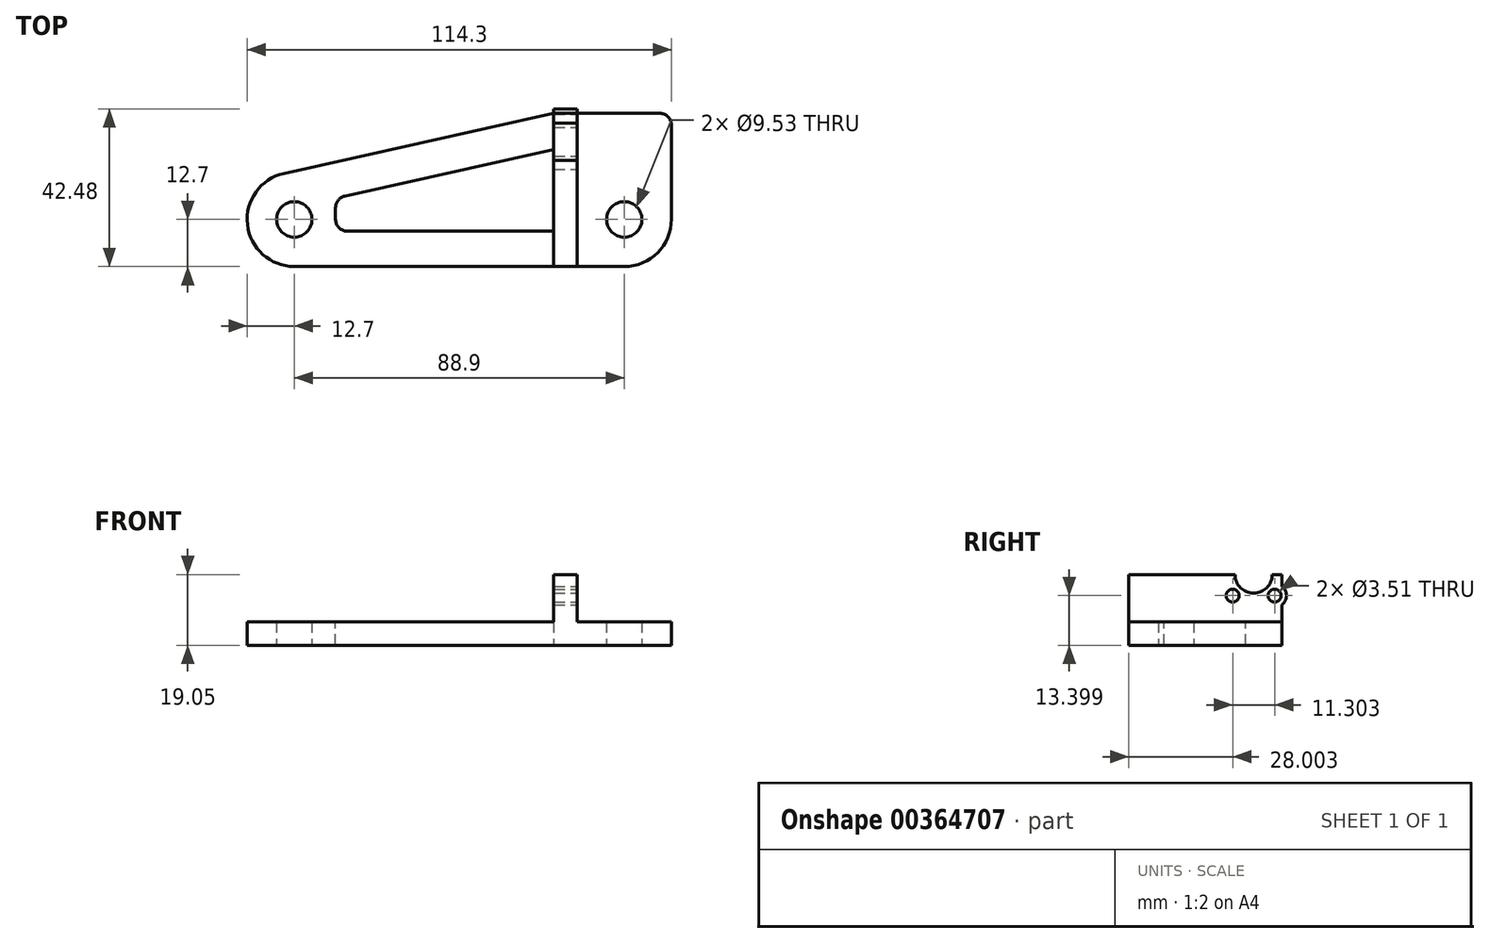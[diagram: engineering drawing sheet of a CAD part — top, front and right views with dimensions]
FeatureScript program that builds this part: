
annotation { "Feature Type Name" : "Feature", "Feature Type Description" : "" }
export const myFeature = defineFeature(function(context is Context, id is Id, definition is map)
    precondition{}
    {
        {
            var Q0;
            Q0=qCreatedBy(makeId("Top.planeOp"),FACE);
            var sketch = newSketch(context, id + "F0", { "sketchPlane" : qUnion([Q0])});
            skCircle(sketch, "E0", {"center": v(0, 0) * mm, "radius": 4.76 * mm});
            skCircle(sketch, "E1", {"center": v(-88.9, 0) * mm, "radius": 4.76 * mm});
            skLineSegment(sketch, "E2", {"start": v(12.7, -12.7) * mm, "end": v(-101.6, -12.7) * mm});
            skLineSegment(sketch, "E3", {"start": v(-101.6, -12.7) * mm, "end": v(-101.6, 10.18) * mm});
            skLineSegment(sketch, "E4", {"start": v(-101.6, 10.18) * mm, "end": v(-19.05, 28.58) * mm});
            skLineSegment(sketch, "E5", {"start": v(-19.05, 28.58) * mm, "end": v(12.7, 28.58) * mm});
            skLineSegment(sketch, "E6", {"start": v(12.7, 28.58) * mm, "end": v(12.7, -12.7) * mm});
            skSolve(sketch);
        }
        {
            var Q0;
            Q0 = qSketchRegion(id + "F0", true);
            extrude(context, id + "F1", {"entities" : qUnion([Q0]), "depth" : 6.35 * mm, "offsetDistance" : 25.4 * mm});
        }
        {
            var Q0;
            Q0=makeQuery(id+"F1.opExtrude","SWEPT_EDGE",EDGE,{"disambiguationData":[OSD([sQuery(id+"F0.wireOp",EDGE,"E2"),sQuery(id+"F0.wireOp",EDGE,"E6")])]});
            var Q1;
            Q1=makeQuery(id+"F1.opExtrude","SWEPT_EDGE",EDGE,{"disambiguationData":[OSD([sQuery(id+"F0.wireOp",EDGE,"E2"),sQuery(id+"F0.wireOp",EDGE,"E3")])]});
            var Q2;
            Q2=makeQuery(id+"F1.opExtrude","SWEPT_EDGE",EDGE,{"disambiguationData":[OSD([sQuery(id+"F0.wireOp",EDGE,"E3"),sQuery(id+"F0.wireOp",EDGE,"E4")])]});
            fillet(context, id + "F2", {"entities" : qUnion([Q0, Q1, Q2]), "radius" : 12.7 * mm, "tangentPropagation" : true, "allowEdgeOverflow" : false});
        }
        {
            var Q0;
            Q0=makeQuery(id+"F1.opExtrude","CAP_FACE",FACE,{"disambiguationData":[OSD([sQuery(id+"F0.wireOp",EDGE,"E0"),sQuery(id+"F0.wireOp",EDGE,"E1"),sQuery(id+"F0.wireOp",EDGE,"E2"),sQuery(id+"F0.wireOp",EDGE,"E3"),sQuery(id+"F0.wireOp",EDGE,"E4"),sQuery(id+"F0.wireOp",EDGE,"E5"),sQuery(id+"F0.wireOp",EDGE,"E6")])],"isStart":false});
            var sketch = newSketch(context, id + "F3", { "sketchPlane" : qUnion([Q0])});
            skLineSegment(sketch, "E7.bottom", {"start": v(-19.05, 28.58) * mm, "end": v(-12.7, 28.58) * mm});
            skLineSegment(sketch, "E7.top", {"start": v(-19.05, -12.7) * mm, "end": v(-12.7, -12.7) * mm});
            skLineSegment(sketch, "E7.left", {"start": v(-19.05, 28.58) * mm, "end": v(-19.05, -12.7) * mm});
            skLineSegment(sketch, "E7.right", {"start": v(-12.7, 28.58) * mm, "end": v(-12.7, -12.7) * mm});
            skSolve(sketch);
        }
        {
            var Q0;
            Q0 = qSketchRegion(id + "F3", true);
            extrude(context, id + "F4", {"entities" : qUnion([Q0]), "operationType" : NewBodyOperationType.ADD, "depth" : 12.7 * mm, "offsetDistance" : 25.4 * mm});
        }
        {
            var Q0;
            {var subQ0=sQuery(id+"F0.wireOp",EDGE,"E4");var subQ1=sQuery(id+"F0.wireOp",EDGE,"E3");var subQ2=sQuery(id+"F0.wireOp",EDGE,"E2");var subQ3=sQuery(id+"F0.wireOp",EDGE,"E1");var subQ4=sQuery(id+"F0.wireOp",EDGE,"E5");Q0=makeQuery(id+"F4.boolean.opBoolean","SPLIT",FACE,{"disambiguationData":[TD([makeQuery(id+"F1.opExtrude","SWEPT_FACE",FACE,{"disambiguationData":[OSD([subQ3])]})])],"derivedFrom":makeQuery(id+"F1.opExtrude","CAP_FACE",FACE,{"disambiguationData":[OSD([sQuery(id+"F0.wireOp",EDGE,"E0"),subQ3,subQ2,subQ1,subQ0,subQ4,sQuery(id+"F0.wireOp",EDGE,"E6")])],"isStart":false})});}
            var sketch = newSketch(context, id + "F5", { "sketchPlane" : qUnion([Q0])});
            skLineSegment(sketch, "E8", {"start": v(-75.3, 6.28) * mm, "end": v(-19.05, 18.82) * mm});
            skLineSegment(sketch, "E9", {"start": v(-19.05, 18.82) * mm, "end": v(-19.05, -3.18) * mm});
            skLineSegment(sketch, "E10", {"start": v(-19.05, -3.18) * mm, "end": v(-74.61, -3.18) * mm});
            skLineSegment(sketch, "E11", {"start": v(-77.79, 0) * mm, "end": v(-77.79, 3.18) * mm});
            skPoint(sketch, "E12.visualSharp", {"position": v(-77.79, 5.73) * mm});
            skArc(sketch, "E12.filletArc", {"start": v(-75.3, 6.28) * mm, "mid": v(-77.09, 5.17) * mm, "end": v(-77.79, 3.18) * mm});
            skPoint(sketch, "E13.visualSharp", {"position": v(-77.79, -3.18) * mm});
            skArc(sketch, "E13.filletArc", {"start": v(-77.79, 0) * mm, "mid": v(-76.86, -2.25) * mm, "end": v(-74.61, -3.18) * mm});
            skSolve(sketch);
        }
        {
            var Q0;
            Q0 = qSketchRegion(id + "F5", true);
            extrude(context, id + "F6", {"entities" : qUnion([Q0]), "operationType" : NewBodyOperationType.REMOVE, "oppositeDirection" : true, "depth" : 25.4 * mm, "offsetDistance" : 25.4 * mm});
        }
        {
            var Q0;
            Q0=makeQuery(id+"F1.opExtrude","SWEPT_EDGE",EDGE,{"disambiguationData":[OSD([sQuery(id+"F0.wireOp",EDGE,"E5"),sQuery(id+"F0.wireOp",EDGE,"E6")])]});
            fillet(context, id + "F7", {"entities" : qUnion([Q0]), "radius" : 3.17 * mm, "tangentPropagation" : true, "allowEdgeOverflow" : false});
        }
        {
            var Q0;
            Q0=makeQuery(id+"F4.opExtrude","SWEPT_FACE",FACE,{"disambiguationData":[OSD([sQuery(id+"F3.wireOp",EDGE,"E7.right")])]});
            var sketch = newSketch(context, id + "F8", { "sketchPlane" : qUnion([Q0])});
            skCircle(sketch, "E14", {"center": v(20.96, 19.05) * mm, "radius": 5 * mm});
            skLineSegment(sketch, "E15.bottom", {"start": v(26.6, 24.7) * mm, "end": v(15.3, 24.7) * mm, "construction": true});
            skLineSegment(sketch, "E15.top", {"start": v(26.6, 13.4) * mm, "end": v(15.3, 13.4) * mm, "construction": true});
            skLineSegment(sketch, "E15.left", {"start": v(26.6, 24.7) * mm, "end": v(26.6, 13.4) * mm, "construction": true});
            skLineSegment(sketch, "E15.right", {"start": v(15.3, 24.7) * mm, "end": v(15.3, 13.4) * mm, "construction": true});
            skCircle(sketch, "E16", {"center": v(26.6, 13.4) * mm, "radius": 1.75 * mm});
            skCircle(sketch, "E17", {"center": v(15.3, 13.4) * mm, "radius": 1.75 * mm});
            skSolve(sketch);
        }
        {
            var Q0;
            Q0 = qSketchRegion(id + "F8", true);
            extrude(context, id + "F9", {"entities" : qUnion([Q0]), "operationType" : NewBodyOperationType.REMOVE, "oppositeDirection" : true, "depth" : 25.4 * mm, "offsetDistance" : 25.4 * mm});
        }
        {
            var Q0;
            Q0=makeQuery(id+"F4.opExtrude","SWEPT_FACE",FACE,{"disambiguationData":[OSD([sQuery(id+"F3.wireOp",EDGE,"E7.right")])]});
            var sketch = newSketch(context, id + "F10", { "sketchPlane" : qUnion([Q0])});
            skArc(sketch, "E18", {"start": v(28.58, 10.9) * mm, "mid": v(29.78, 13.4) * mm, "end": v(28.58, 15.89) * mm});
            skLineSegment(sketch, "E19", {"start": v(28.58, 15.89) * mm, "end": v(28.58, 10.9) * mm});
            skSolve(sketch);
        }
        {
            var Q0;
            Q0 = qSketchRegion(id + "F10", true);
            extrude(context, id + "F11", {"entities" : qUnion([Q0]), "operationType" : NewBodyOperationType.ADD, "oppositeDirection" : true, "depth" : 6.35 * mm, "offsetDistance" : 25.4 * mm});
        }
    });
